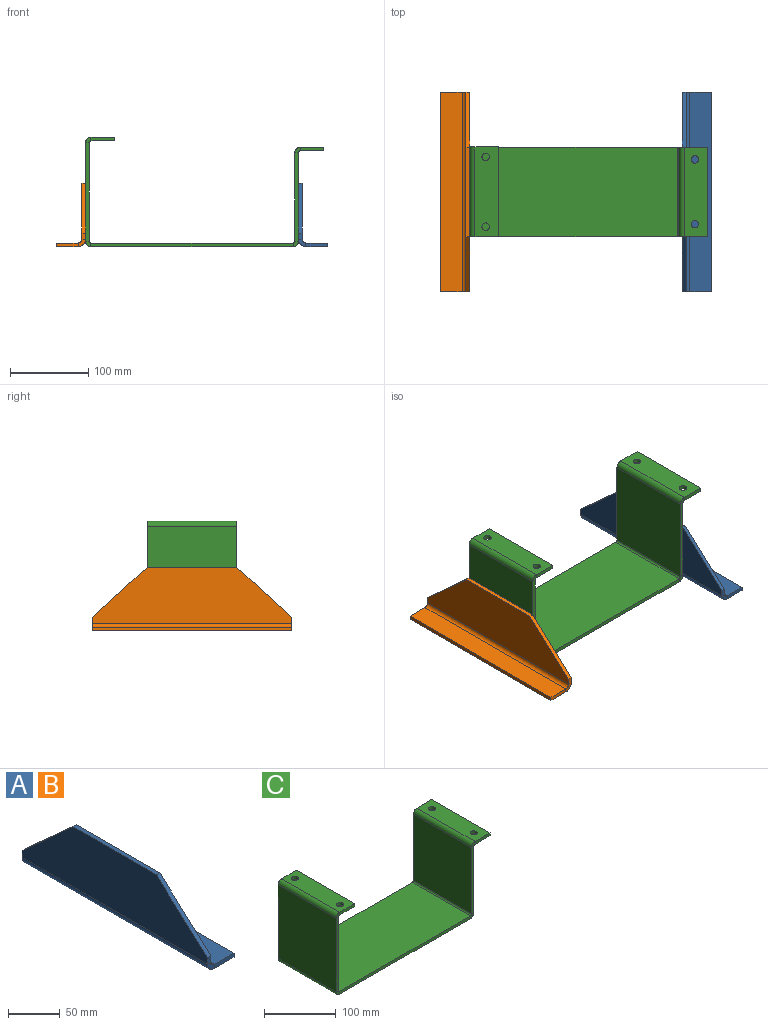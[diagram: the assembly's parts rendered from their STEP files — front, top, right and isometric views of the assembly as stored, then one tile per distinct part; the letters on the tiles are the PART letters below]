
ASSEMBLY  parts=3 mates=5
PART A: 16 faces, bbox 36.5x254x81 mm
  f0: plane 7.92x4.76mm, normal (0,-1,0), area 37.7mm2, adj f1,f5,f6,f12
  f1: plane 69.85x63.5mm, normal (0,-0.67,0.74), area 449.6mm2, adj f0,f2,f5,f6
  f2: plane 114.3x4.76mm, normal (0,0,1), area 544.4mm2, adj f1,f3,f5,f6
  f3: plane 69.85x63.5mm, normal (0,0.67,0.74), area 449.6mm2, adj f2,f4,f5,f6
  f4: plane 7.92x4.76mm, normal (0,1,0), area 37.7mm2, adj f3,f5,f6,f13
  f5: plane 254x71.43mm, normal (-1,0,0), area 13706.4mm2, adj f0,f1,f2,f3,f4,f14
  f6: plane 254x71.43mm, normal (1,0,0), area 13706.4mm2, adj f0,f1,f2,f3,f4,f15
  f7: plane 26.98x4.76mm, normal (0,1,0), area 128.5mm2, adj f8,f10,f11,f13
  f8: plane 254x4.76mm, normal (1,0,0), area 1209.7mm2, adj f7,f9,f10,f11
  f9: plane 26.98x4.76mm, normal (0,-1,0), area 128.5mm2, adj f8,f10,f11,f12
  f10: plane 254x26.98mm, normal (0,0,-1), area 6851.6mm2, adj f7,f8,f9,f14
  f11: plane 254x26.98mm, normal (0,0,1), area 6851.6mm2, adj f7,f8,f9,f15
  f12: plane 9.54x9.54mm, normal (0,-1,0), area 53.5mm2, adj f0,f9,f14,f15
  f13: plane 9.54x9.54mm, normal (0,1,0), area 53.5mm2, adj f4,f7,f14,f15
  f14: cylinder r=9.54mm len=254mm, axis (0,-1,0), area 3805.4mm2, adj f5,f10,f12,f13
  f15: cylinder r=4.78mm len=254mm, axis (0,-1,0), area 1905.2mm2, adj f6,f11,f12,f13
PART B: same geometry as A
PART C: 42 faces, bbox 303.2x114.3x139.7 mm
  f0: plane 29.53x4.76mm, normal (0,1,0), area 140.6mm2, adj f1,f5,f6,f39
  f1: plane 114.3x4.76mm, normal (1,0,0), area 544.4mm2, adj f0,f2,f5,f6
  f2: plane 29.53x4.76mm, normal (0,-1,0), area 140.6mm2, adj f1,f5,f6,f38
  f3: cylinder r=4.76mm len=9.53mm, axis (0,0,-1), area 142.5mm2, adj f5,f6
  f4: cylinder r=4.76mm len=9.53mm, axis (0,0,-1), area 142.5mm2, adj f5,f6
  f5: plane 114.3x29.53mm, normal (0,0,-1), area 3232.5mm2, adj f0,f1,f2,f3,f4,f41
  f6: plane 114.3x29.53mm, normal (0,0,1), area 3232.5mm2, adj f0,f1,f2,f3,f4,f40
  f7: plane 125.73x4.76mm, normal (0,1,0), area 598.8mm2, adj f9,f10,f35,f39
  f8: plane 125.73x4.76mm, normal (0,-1,0), area 598.8mm2, adj f9,f10,f34,f38
  f9: plane 125.73x114.3mm, normal (1,0,0), area 14370.9mm2, adj f7,f8,f37,f41
  f10: plane 125.73x114.3mm, normal (-1,0,0), area 14370.9mm2, adj f7,f8,f36,f40
  f11: plane 257.49x4.76mm, normal (0,1,0), area 1226.3mm2, adj f13,f14,f31,f35
  f12: plane 257.49x4.76mm, normal (0,-1,0), area 1226.3mm2, adj f13,f14,f30,f34
  f13: plane 257.49x114.3mm, normal (0,0,1), area 29431.4mm2, adj f11,f12,f33,f37
  f14: plane 257.49x114.3mm, normal (0,0,-1), area 29431.4mm2, adj f11,f12,f32,f36
  f15: plane 113.03x4.76mm, normal (0,1,0), area 538.3mm2, adj f17,f18,f27,f31
  f16: plane 113.03x4.76mm, normal (0,-1,0), area 538.3mm2, adj f17,f18,f26,f30
  f17: plane 114.3x113.03mm, normal (-1,0,0), area 12919.3mm2, adj f15,f16,f28,f33
  f18: plane 114.3x113.03mm, normal (1,0,0), area 12919.3mm2, adj f15,f16,f29,f32
  f19: plane 29.53x4.76mm, normal (0,1,0), area 140.6mm2, adj f23,f24,f25,f27
  f20: plane 29.53x4.76mm, normal (0,-1,0), area 140.6mm2, adj f23,f24,f25,f26
  f21: cylinder r=4.76mm len=9.53mm, axis (0,0,1), area 142.5mm2, adj f24,f25
  f22: cylinder r=4.76mm len=9.53mm, axis (0,0,1), area 142.5mm2, adj f24,f25
  f23: plane 114.3x4.76mm, normal (1,0,0), area 544.4mm2, adj f19,f20,f24,f25
  f24: plane 114.3x29.53mm, normal (0,0,1), area 3232.5mm2, adj f19,f20,f21,f22,f23,f28
  f25: plane 114.3x29.53mm, normal (0,0,-1), area 3232.5mm2, adj f19,f20,f21,f22,f23,f29
  f26: plane 6.99x6.99mm, normal (0,-1,0), area 34.4mm2, adj f16,f20,f28,f29
  f27: plane 6.99x6.99mm, normal (0,1,0), area 34.4mm2, adj f15,f19,f28,f29
  f28: cylinder r=6.99mm len=114.3mm, axis (0,-1,0), area 1254.1mm2, adj f17,f24,f26,f27
  f29: cylinder r=2.22mm len=114.3mm, axis (0,-1,0), area 399mm2, adj f18,f25,f26,f27
  f30: plane 6.99x6.99mm, normal (0,-1,0), area 34.4mm2, adj f12,f16,f32,f33
  f31: plane 6.99x6.99mm, normal (0,1,0), area 34.4mm2, adj f11,f15,f32,f33
  f32: cylinder r=6.99mm len=114.3mm, axis (0,-1,0), area 1254.1mm2, adj f14,f18,f30,f31
  f33: cylinder r=2.22mm len=114.3mm, axis (0,-1,0), area 399mm2, adj f13,f17,f30,f31
  f34: plane 6.99x6.99mm, normal (0,-1,0), area 34.4mm2, adj f8,f12,f36,f37
  f35: plane 6.99x6.99mm, normal (0,1,0), area 34.4mm2, adj f7,f11,f36,f37
  f36: cylinder r=6.99mm len=114.3mm, axis (0,-1,0), area 1254.1mm2, adj f10,f14,f34,f35
  f37: cylinder r=2.22mm len=114.3mm, axis (0,-1,0), area 399mm2, adj f9,f13,f34,f35
  f38: plane 6.99x6.99mm, normal (0,-1,0), area 34.4mm2, adj f2,f8,f40,f41
  f39: plane 6.99x6.99mm, normal (0,1,0), area 34.4mm2, adj f0,f7,f40,f41
  f40: cylinder r=6.99mm len=114.3mm, axis (0,-1,0), area 1254.1mm2, adj f6,f10,f38,f39
  f41: cylinder r=2.22mm len=114.3mm, axis (0,-1,0), area 399mm2, adj f5,f9,f38,f39
PLACE A t=(276.23,57.15,4.76)mm fixed
PLACE B rot(axis=(0,0,1),180deg) t=(-4.76,57.15,4.76)mm
PLACE C t=(0,114.3,0)mm
MATE planar C.f18 <-> A.f5  axis (1,0,0) through (271.46,57.15,63.5)mm
MATE planar B.f7 <-> A.f9  axis (0,-1,0) through (-23.03,-69.85,2.38)mm
MATE planar C.f14 <-> A.f10  axis (0,0,-1) through (264.48,57.15,0)mm
MATE planar B.f5 <-> C.f10  axis (1,0,0) through (0,57.15,40.54)mm
MATE planar B.f10 <-> C.f14  axis (0,0,-1) through (-23.03,57.15,0)mm
